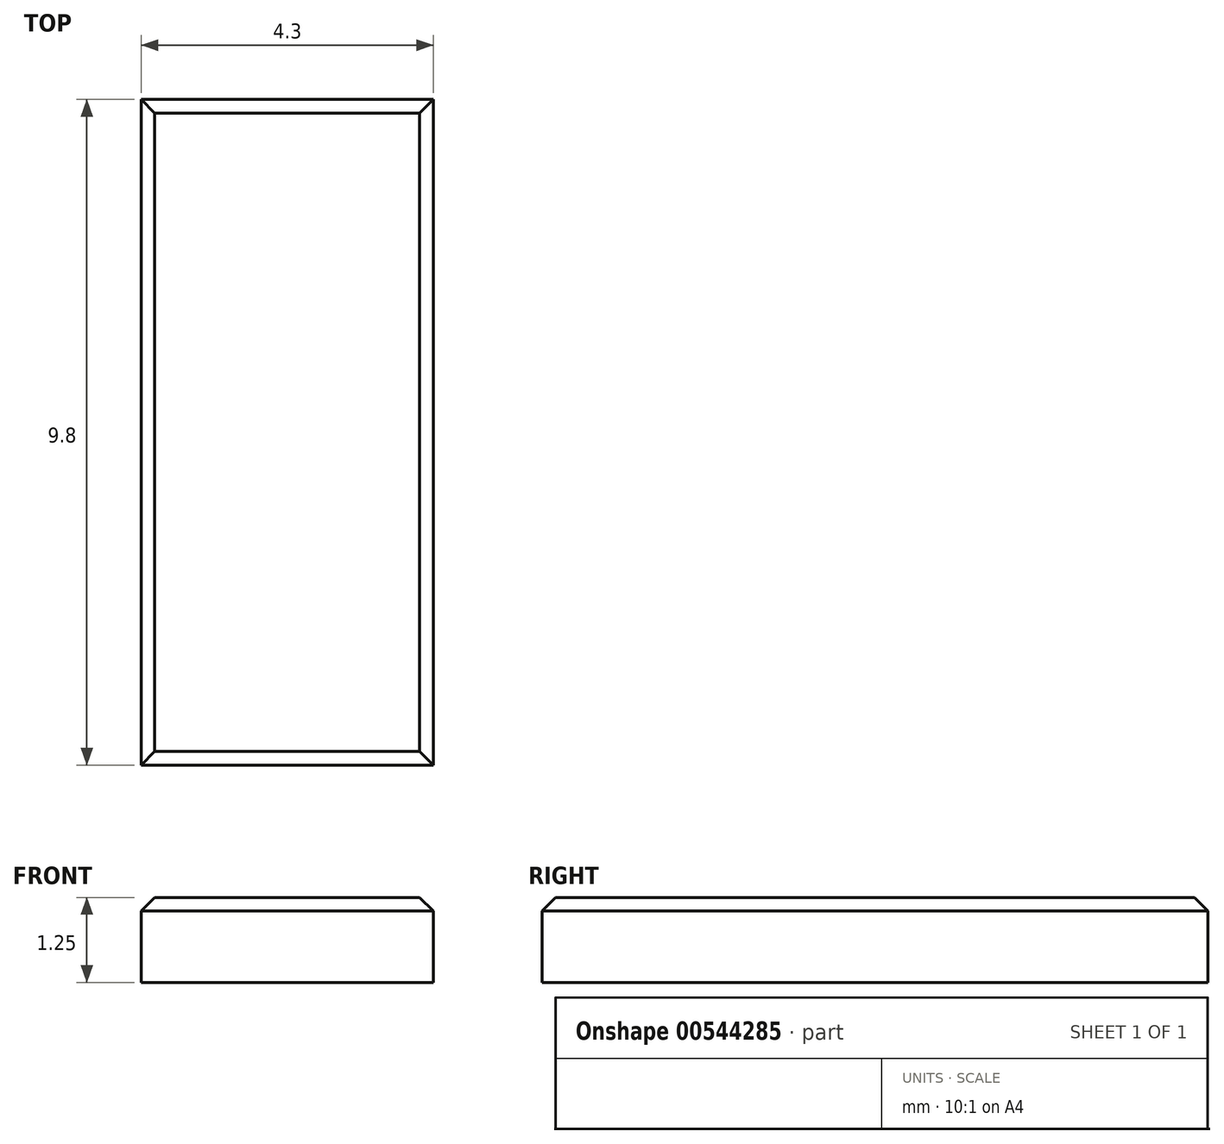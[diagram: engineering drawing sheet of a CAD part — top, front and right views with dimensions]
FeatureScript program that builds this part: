
annotation { "Feature Type Name" : "Feature", "Feature Type Description" : "" }
export const myFeature = defineFeature(function(context is Context, id is Id, definition is map)
    precondition{}
    {
        {
            var Q0;
            Q0=qCreatedBy(makeId("Top.planeOp"),FACE);
            var sketch = newSketch(context, id + "F0", { "sketchPlane" : qUnion([Q0])});
            skLineSegment(sketch, "E0.bottom", {"start": v(0, 0) * mm, "end": v(4.3, 0) * mm});
            skLineSegment(sketch, "E0.top", {"start": v(0, 9.8) * mm, "end": v(4.3, 9.8) * mm});
            skLineSegment(sketch, "E0.left", {"start": v(0, 0) * mm, "end": v(0, 9.8) * mm});
            skLineSegment(sketch, "E0.right", {"start": v(4.3, 0) * mm, "end": v(4.3, 9.8) * mm});
            skSolve(sketch);
        }
        {
            var Q0;
            Q0=qSketchRegion(id+"F0",true);
            extrude(context, id + "F1", {"entities" : qUnion([Q0]), "depth" : 1.25 * mm});
        }
        {
            var Q0;
            Q0=makeQuery(id+"F1.opExtrude","CAP_EDGE",EDGE,{"disambiguationData":[OSD([sQuery(id+"F0.wireOp",EDGE,"E0.top")])],"isStart":false});
            var Q1;
            Q1=makeQuery(id+"F1.opExtrude","CAP_EDGE",EDGE,{"disambiguationData":[OSD([sQuery(id+"F0.wireOp",EDGE,"E0.left")])],"isStart":false});
            var Q2;
            Q2=makeQuery(id+"F1.opExtrude","CAP_EDGE",EDGE,{"disambiguationData":[OSD([sQuery(id+"F0.wireOp",EDGE,"E0.right")])],"isStart":false});
            var Q3;
            Q3=makeQuery(id+"F1.opExtrude","CAP_EDGE",EDGE,{"disambiguationData":[OSD([sQuery(id+"F0.wireOp",EDGE,"E0.bottom")])],"isStart":false});
            chamfer(context, id + "F2", {"entities" : qUnion([Q0, Q1, Q2, Q3]), "width" : 0.2 * mm, "tangentPropagation" : true});
        }
    });
